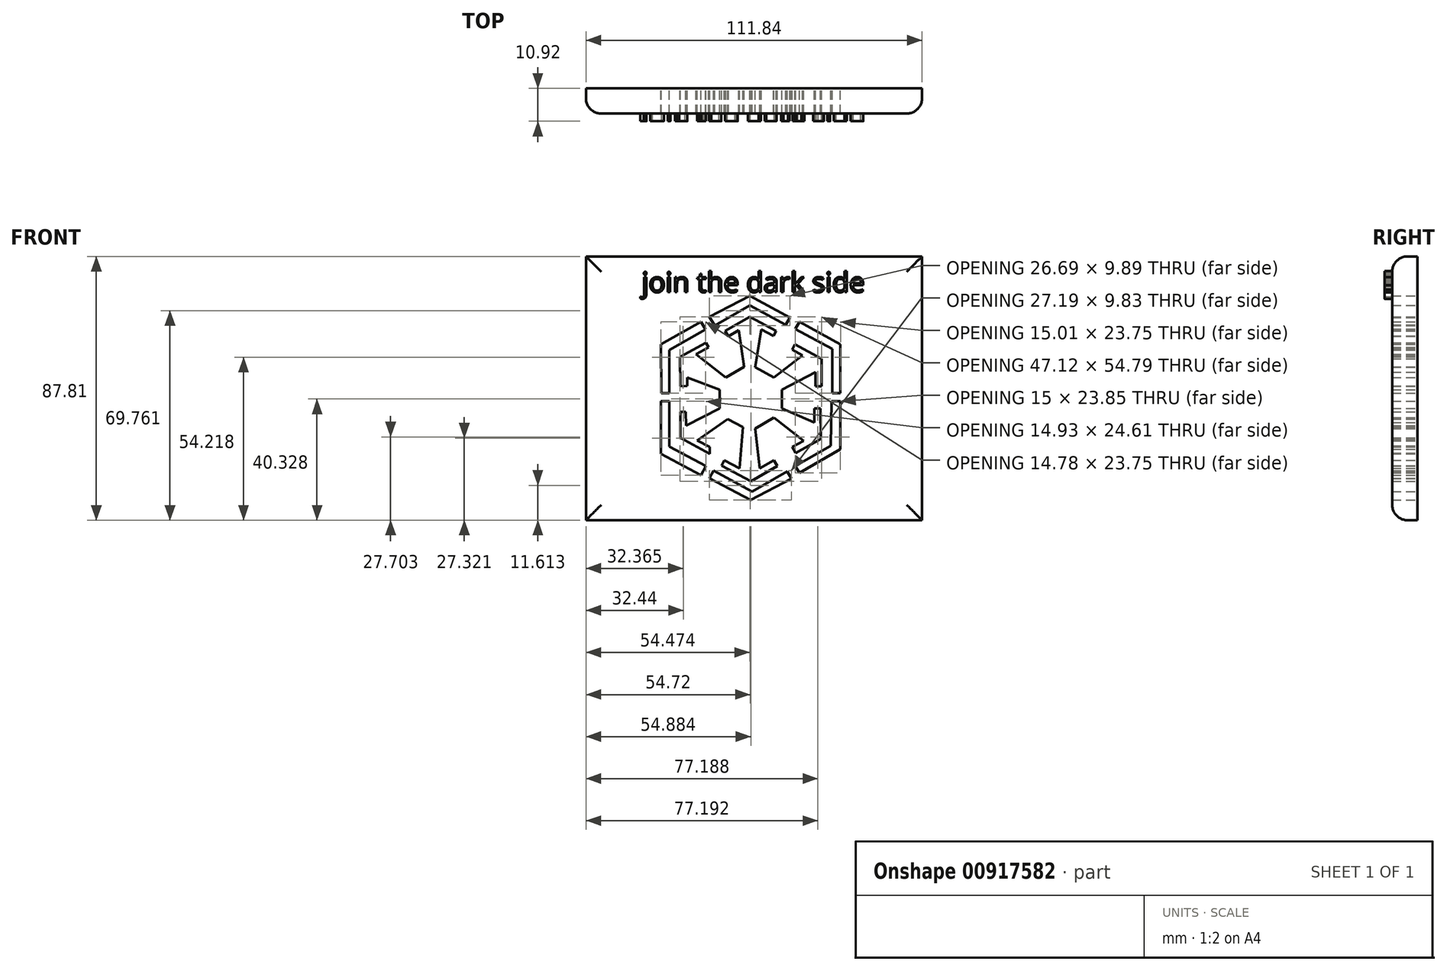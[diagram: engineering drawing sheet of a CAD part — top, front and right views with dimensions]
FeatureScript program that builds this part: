
annotation { "Feature Type Name" : "Feature", "Feature Type Description" : "" }
export const myFeature = defineFeature(function(context is Context, id is Id, definition is map)
    precondition{}
    {
        {
            var Q0;
            Q0=qCreatedBy(makeId("Front.planeOp"),FACE);
            var sketch = newSketch(context, id + "F0", { "sketchPlane" : qUnion([Q0])});
            skLineSegment(sketch, "E0", {"start": v(-31.28, 25.92) * mm, "end": v(-17.98, 33.52) * mm});
            skLineSegment(sketch, "E1", {"start": v(-17.98, 33.52) * mm, "end": v(-16.5, 30.94) * mm});
            skLineSegment(sketch, "E2", {"start": v(-16.5, 30.94) * mm, "end": v(-28.5, 24.09) * mm});
            skLineSegment(sketch, "E3", {"start": v(-28.5, 24.09) * mm, "end": v(-28.5, 9.77) * mm});
            skLineSegment(sketch, "E4", {"start": v(-28.5, 9.77) * mm, "end": v(-31.15, 9.77) * mm});
            skLineSegment(sketch, "E5", {"start": v(-31.15, 9.77) * mm, "end": v(-31.28, 25.92) * mm});
            skLineSegment(sketch, "E6", {"start": v(-15.13, 35.15) * mm, "end": v(-13.47, 32.24) * mm});
            skLineSegment(sketch, "E7", {"start": v(-13.47, 32.24) * mm, "end": v(-1.68, 38.98) * mm});
            skLineSegment(sketch, "E8", {"start": v(-1.68, 38.98) * mm, "end": v(10.25, 32.44) * mm});
            skLineSegment(sketch, "E9", {"start": v(10.25, 32.44) * mm, "end": v(11.56, 34.83) * mm});
            skLineSegment(sketch, "E10", {"start": v(11.56, 34.83) * mm, "end": v(-1.75, 42.14) * mm});
            skLineSegment(sketch, "E11", {"start": v(-1.75, 42.14) * mm, "end": v(-15.13, 35.15) * mm});
            skLineSegment(sketch, "E12", {"start": v(-31.28, 7.06) * mm, "end": v(-28.5, 7.06) * mm});
            skLineSegment(sketch, "E13", {"start": v(-28.5, 7.06) * mm, "end": v(-28.5, -8) * mm});
            skLineSegment(sketch, "E14", {"start": v(-28.5, -8) * mm, "end": v(-16.35, -14.52) * mm});
            skLineSegment(sketch, "E15", {"start": v(-16.35, -14.52) * mm, "end": v(-17.98, -17.56) * mm});
            skLineSegment(sketch, "E16", {"start": v(-17.98, -17.56) * mm, "end": v(-31.28, -10.42) * mm});
            skLineSegment(sketch, "E17", {"start": v(-31.28, -10.42) * mm, "end": v(-31.28, 7.06) * mm});
            skLineSegment(sketch, "E18", {"start": v(-13.78, -16.04) * mm, "end": v(-15.13, -18.57) * mm});
            skPoint(sketch, "E18.startSnap0", {"position": v(-17.17, -16.04) * mm});
            skLineSegment(sketch, "E19", {"start": v(-15.13, -18.57) * mm, "end": v(-1.52, -25.87) * mm});
            skLineSegment(sketch, "E20", {"start": v(-1.52, -25.87) * mm, "end": v(12.05, -18.79) * mm});
            skLineSegment(sketch, "E21", {"start": v(12.05, -18.79) * mm, "end": v(10.67, -16.36) * mm});
            skLineSegment(sketch, "E22", {"start": v(10.67, -16.36) * mm, "end": v(-1, -23.02) * mm});
            skLineSegment(sketch, "E23", {"start": v(-1, -23.02) * mm, "end": v(-13.78, -16.04) * mm});
            skLineSegment(sketch, "E24", {"start": v(14.73, 33.52) * mm, "end": v(13.42, 31.1) * mm});
            skLineSegment(sketch, "E25", {"start": v(13.42, 31.1) * mm, "end": v(25.76, 24.47) * mm});
            skLineSegment(sketch, "E26", {"start": v(25.76, 24.47) * mm, "end": v(25.76, 9.77) * mm});
            skLineSegment(sketch, "E27", {"start": v(25.76, 9.77) * mm, "end": v(28.43, 9.77) * mm});
            skLineSegment(sketch, "E28", {"start": v(28.43, 9.77) * mm, "end": v(28.43, 25.92) * mm});
            skLineSegment(sketch, "E29", {"start": v(28.43, 25.92) * mm, "end": v(14.73, 33.52) * mm});
            skLineSegment(sketch, "E30", {"start": v(25.45, 7.06) * mm, "end": v(28.43, 7.06) * mm});
            skLineSegment(sketch, "E31", {"start": v(28.43, 7.06) * mm, "end": v(28.43, -8.96) * mm});
            skLineSegment(sketch, "E32", {"start": v(28.43, -8.96) * mm, "end": v(14.73, -16.8) * mm});
            skLineSegment(sketch, "E33", {"start": v(14.73, -16.8) * mm, "end": v(13.43, -14.52) * mm});
            skLineSegment(sketch, "E34", {"start": v(13.43, -14.52) * mm, "end": v(25.25, -7.77) * mm});
            skLineSegment(sketch, "E35", {"start": v(25.25, -7.77) * mm, "end": v(25.45, 7.06) * mm});
            skLineSegment(sketch, "E36", {"start": v(-5.36, 30.67) * mm, "end": v(-8.9, 28.65) * mm});
            skLineSegment(sketch, "E37", {"start": v(-8.9, 28.65) * mm, "end": v(-9.93, 30.47) * mm});
            skLineSegment(sketch, "E38", {"start": v(-9.93, 30.47) * mm, "end": v(-1.73, 35.15) * mm});
            skLineSegment(sketch, "E39", {"start": v(-1.73, 35.15) * mm, "end": v(7.1, 30.42) * mm});
            skLineSegment(sketch, "E40", {"start": v(7.1, 30.42) * mm, "end": v(6.2, 28.74) * mm});
            skLineSegment(sketch, "E41", {"start": v(6.2, 28.74) * mm, "end": v(2.04, 30.97) * mm});
            skLineSegment(sketch, "E42", {"start": v(2.04, 30.97) * mm, "end": v(0, 18.32) * mm});
            skLineSegment(sketch, "E43", {"start": v(0, 18.32) * mm, "end": v(6.26, 14.96) * mm});
            skLineSegment(sketch, "E44", {"start": v(6.26, 14.96) * mm, "end": v(15.81, 22.26) * mm});
            skLineSegment(sketch, "E45", {"start": v(15.81, 22.26) * mm, "end": v(12.31, 24.14) * mm});
            skLineSegment(sketch, "E46", {"start": v(12.31, 24.14) * mm, "end": v(13.27, 25.92) * mm});
            skLineSegment(sketch, "E47", {"start": v(13.27, 25.92) * mm, "end": v(22.18, 21.14) * mm});
            skLineSegment(sketch, "E48", {"start": v(22.18, 21.14) * mm, "end": v(22.18, 11.94) * mm});
            skLineSegment(sketch, "E49", {"start": v(22.18, 11.94) * mm, "end": v(20.16, 11.94) * mm});
            skLineSegment(sketch, "E50", {"start": v(20.16, 11.94) * mm, "end": v(20.16, 16.7) * mm});
            skLineSegment(sketch, "E51", {"start": v(20.16, 16.7) * mm, "end": v(8.92, 10.83) * mm});
            skLineSegment(sketch, "E52", {"start": v(8.92, 10.83) * mm, "end": v(8.92, 4.61) * mm});
            skLineSegment(sketch, "E53", {"start": v(8.92, 4.61) * mm, "end": v(19.75, 0) * mm});
            skLineSegment(sketch, "E54", {"start": v(19.75, 0) * mm, "end": v(19.7, 4.61) * mm});
            skLineSegment(sketch, "E55", {"start": v(19.7, 4.61) * mm, "end": v(21.79, 4.63) * mm});
            skLineSegment(sketch, "E56", {"start": v(21.79, 4.63) * mm, "end": v(21.88, -5.57) * mm});
            skLineSegment(sketch, "E57", {"start": v(21.88, -5.57) * mm, "end": v(13.5, -10.18) * mm});
            skLineSegment(sketch, "E58", {"start": v(13.5, -10.18) * mm, "end": v(12.42, -8.2) * mm});
            skLineSegment(sketch, "E59", {"start": v(12.42, -8.2) * mm, "end": v(16.17, -6.14) * mm});
            skLineSegment(sketch, "E60", {"start": v(16.17, -6.14) * mm, "end": v(6.26, 1.63) * mm});
            skLineSegment(sketch, "E61", {"start": v(6.26, 1.63) * mm, "end": v(0, -2.04) * mm});
            skLineSegment(sketch, "E62", {"start": v(0, -2.04) * mm, "end": v(1.56, -15.34) * mm});
            skLineSegment(sketch, "E63", {"start": v(1.56, -15.34) * mm, "end": v(6.26, -12.62) * mm});
            skLineSegment(sketch, "E64", {"start": v(6.26, -12.62) * mm, "end": v(7.4, -14.6) * mm});
            skLineSegment(sketch, "E65", {"start": v(7.4, -14.6) * mm, "end": v(-1.33, -19.64) * mm});
            skLineSegment(sketch, "E66", {"start": v(-1.33, -19.64) * mm, "end": v(-11.14, -14.37) * mm});
            skLineSegment(sketch, "E67", {"start": v(-11.14, -14.37) * mm, "end": v(-10.2, -12.62) * mm});
            skLineSegment(sketch, "E68", {"start": v(-10.2, -12.62) * mm, "end": v(-5.15, -15.34) * mm});
            skLineSegment(sketch, "E69", {"start": v(-5.15, -15.34) * mm, "end": v(-4, -1.63) * mm});
            skLineSegment(sketch, "E70", {"start": v(-4, -1.63) * mm, "end": v(-9.15, 1.14) * mm});
            skLineSegment(sketch, "E71", {"start": v(-9.15, 1.14) * mm, "end": v(-19.2, -5.97) * mm});
            skLineSegment(sketch, "E72", {"start": v(-19.2, -5.97) * mm, "end": v(-15.03, -8.22) * mm});
            skLineSegment(sketch, "E73", {"start": v(-15.03, -8.22) * mm, "end": v(-15, -10.44) * mm});
            skLineSegment(sketch, "E74", {"start": v(-15, -10.44) * mm, "end": v(-24.78, -5.2) * mm});
            skLineSegment(sketch, "E75", {"start": v(-24.78, -5.2) * mm, "end": v(-24.85, 3.53) * mm});
            skLineSegment(sketch, "E76", {"start": v(-24.85, 3.53) * mm, "end": v(-23, 3.53) * mm});
            skLineSegment(sketch, "E77", {"start": v(-23, 3.53) * mm, "end": v(-22.97, -1.09) * mm});
            skLineSegment(sketch, "E78", {"start": v(-22.97, -1.09) * mm, "end": v(-11.74, 4.61) * mm});
            skLineSegment(sketch, "E79", {"start": v(-11.74, 4.61) * mm, "end": v(-11.8, 10.83) * mm});
            skLineSegment(sketch, "E80", {"start": v(-11.8, 10.83) * mm, "end": v(-22.6, 14.96) * mm});
            skLineSegment(sketch, "E81", {"start": v(-22.6, 14.96) * mm, "end": v(-22.57, 12.08) * mm});
            skLineSegment(sketch, "E82", {"start": v(-22.57, 12.08) * mm, "end": v(-24.85, 12.06) * mm});
            skLineSegment(sketch, "E83", {"start": v(-24.85, 12.06) * mm, "end": v(-24.93, 21.72) * mm});
            skLineSegment(sketch, "E84", {"start": v(-24.93, 21.72) * mm, "end": v(-16.35, 26.47) * mm});
            skLineSegment(sketch, "E85", {"start": v(-16.35, 26.47) * mm, "end": v(-15.5, 24.93) * mm});
            skLineSegment(sketch, "E86", {"start": v(-15.5, 24.93) * mm, "end": v(-19.62, 22.66) * mm});
            skLineSegment(sketch, "E87", {"start": v(-19.62, 22.66) * mm, "end": v(-9.7, 14.96) * mm});
            skLineSegment(sketch, "E88", {"start": v(-9.7, 14.96) * mm, "end": v(-3.6, 18.46) * mm});
            skLineSegment(sketch, "E89", {"start": v(-3.6, 18.46) * mm, "end": v(-5.36, 30.67) * mm});
            skLineSegment(sketch, "E90.bottom", {"start": v(-56.26, 55.24) * mm, "end": v(55.58, 55.24) * mm});
            skLineSegment(sketch, "E90.top", {"start": v(-56.26, -32.57) * mm, "end": v(55.58, -32.57) * mm});
            skLineSegment(sketch, "E90.left", {"start": v(-56.26, 55.24) * mm, "end": v(-56.26, -32.57) * mm});
            skLineSegment(sketch, "E90.right", {"start": v(55.58, 55.24) * mm, "end": v(55.58, -32.57) * mm});
            skSolve(sketch);
        }
        {
            var Q0;
            Q0 = qSketchRegion(id + "F0", true);
            extrude(context, id + "F1", {"entities" : qUnion([Q0]), "depth" : 8.38 * mm, "offsetDistance" : 25.4 * mm});
        }
        {
            var Q0;
            Q0=qCreatedBy(makeId("Front.planeOp"),FACE);
            var sketch = newSketch(context, id + "F2", { "sketchPlane" : qUnion([Q0])});
            skText(sketch, "E91", { "text": "join the dark side\n", "fontName": "OpenSans-Regular.ttf"});
            const initialGuessF2  = {"E91": [-0.03772, 0.04333, 1, 0, 0.00665]};
            skSetInitialGuess(sketch, initialGuessF2);
            skSolve(sketch);
        }
        {
            var Q0;
            Q0 = qSketchRegion(id + "F2", true);
            extrude(context, id + "F3", {"entities" : qUnion([Q0]), "operationType" : NewBodyOperationType.ADD, "depth" : 10.92 * mm, "offsetDistance" : 25.4 * mm});
        }
        {
            var Q0;
            Q0=makeQuery(id+"F1.opExtrude","CAP_EDGE",EDGE,{"disambiguationData":[OSD([sQuery(id+"F0.wireOp",EDGE,"E90.bottom")])],"isStart":false});
            var Q1;
            Q1=makeQuery(id+"F1.opExtrude","CAP_EDGE",EDGE,{"disambiguationData":[OSD([sQuery(id+"F0.wireOp",EDGE,"E90.left")])],"isStart":false});
            var Q2;
            Q2=makeQuery(id+"F1.opExtrude","CAP_EDGE",EDGE,{"disambiguationData":[OSD([sQuery(id+"F0.wireOp",EDGE,"E90.top")])],"isStart":false});
            var Q3;
            Q3=makeQuery(id+"F1.opExtrude","CAP_EDGE",EDGE,{"disambiguationData":[OSD([sQuery(id+"F0.wireOp",EDGE,"E90.right")])],"isStart":false});
            fillet(context, id + "F4", {"entities" : qUnion([Q0, Q1, Q2, Q3]), "radius" : 5.08 * mm, "tangentPropagation" : true, "allowEdgeOverflow" : false});
        }
    });
